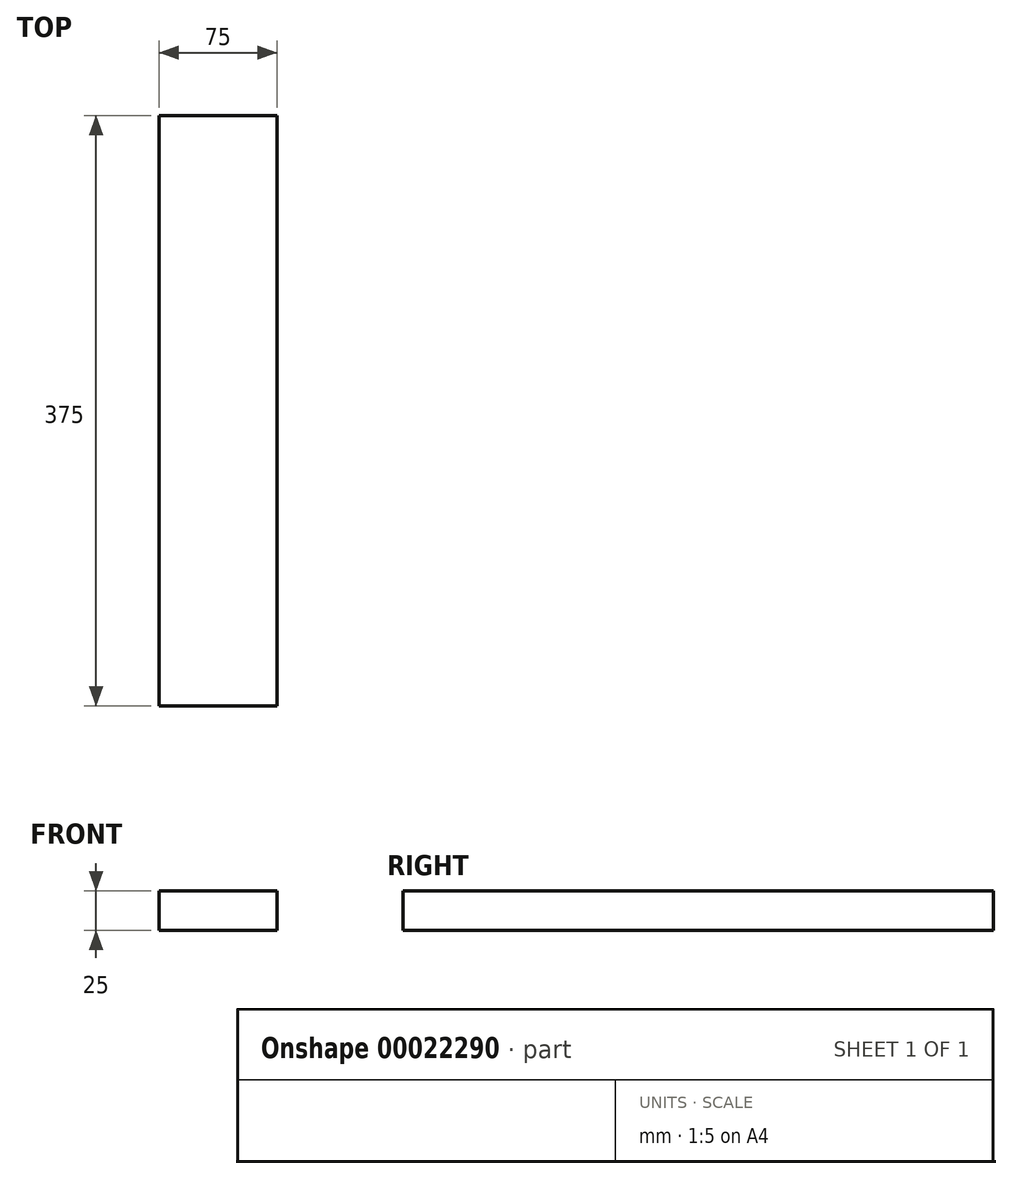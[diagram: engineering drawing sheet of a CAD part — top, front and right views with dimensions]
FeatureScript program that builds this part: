
annotation { "Feature Type Name" : "Feature", "Feature Type Description" : "" }
export const myFeature = defineFeature(function(context is Context, id is Id, definition is map)
    precondition{}
    {
        {
            var Q0;
            Q0=qCreatedBy(makeId("Front.planeOp"),FACE);
            var sketch = newSketch(context, id + "F0", { "sketchPlane" : qUnion([Q0])});
            skLineSegment(sketch, "E0.rect.bottom", {"start": v(37.5, 12.5) * mm, "end": v(-37.5, 12.5) * mm});
            skLineSegment(sketch, "E0.rect.top", {"start": v(37.5, -12.5) * mm, "end": v(-37.5, -12.5) * mm});
            skLineSegment(sketch, "E0.rect.left", {"start": v(37.5, 12.5) * mm, "end": v(37.5, -12.5) * mm});
            skLineSegment(sketch, "E0.rect.right", {"start": v(-37.5, 12.5) * mm, "end": v(-37.5, -12.5) * mm});
            skPoint(sketch, "E0.rect.middle", {"position": v(0, 0) * mm});
            skSolve(sketch);
        }
        {
            var Q0;
            Q0=makeQuery(id+"F0.imprint","IMPRINT",FACE,{"disambiguationData":[TD([[makeQuery(id+"F0.imprint","IMPRINT",EDGE,{"derivedFrom":sQuery(id+"F0.wireOp",EDGE,"E0.rect.bottom")}),1.0]])]});
            extrude(context, id + "F1", {"entities" : qUnion([Q0]), "endBound" : BoundingType.SYMMETRIC, "depth" : 375 * mm});
        }
    });
